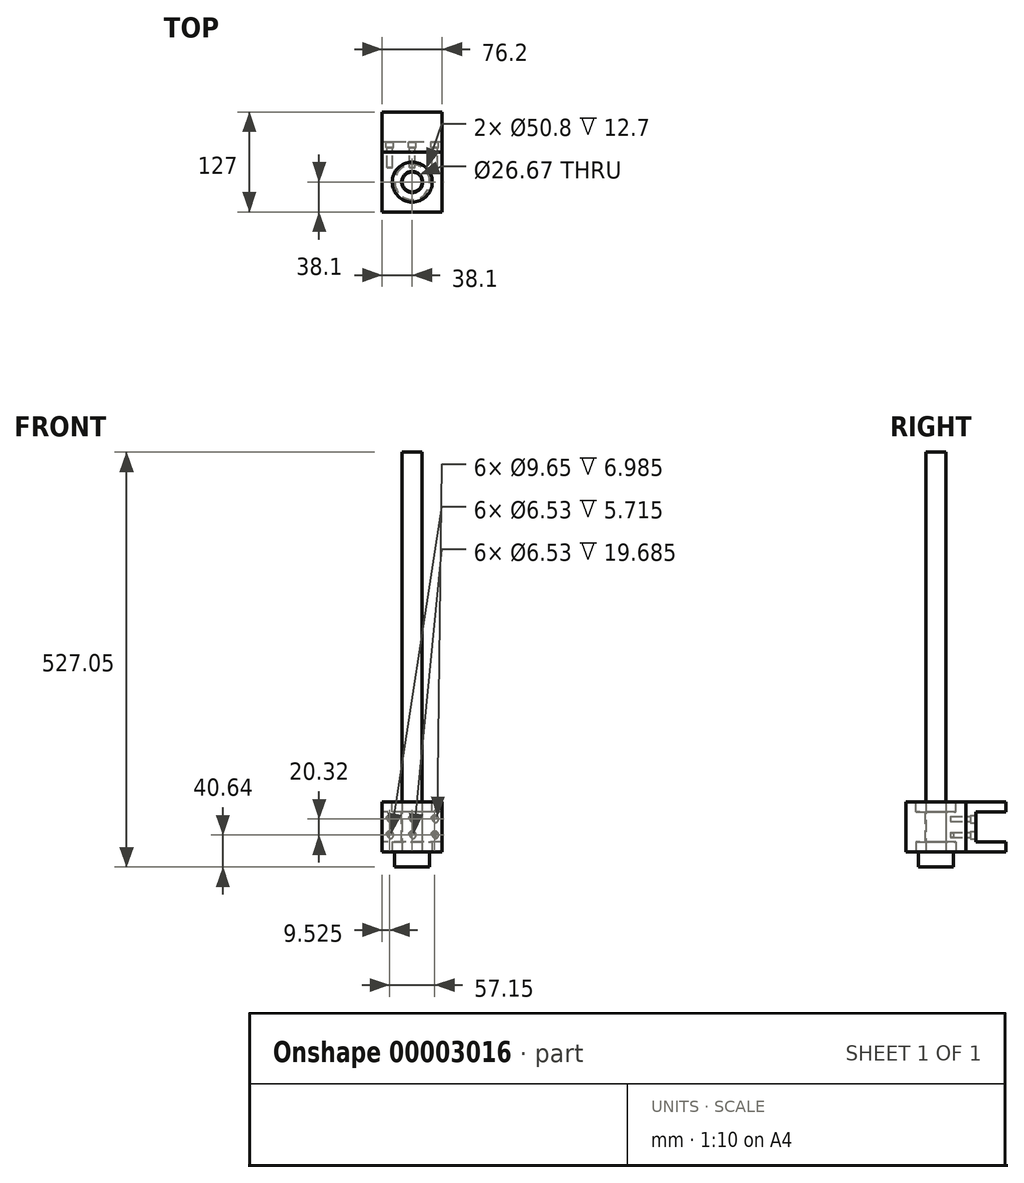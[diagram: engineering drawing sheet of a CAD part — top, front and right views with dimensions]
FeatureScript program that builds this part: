
annotation { "Feature Type Name" : "Feature", "Feature Type Description" : "" }
export const myFeature = defineFeature(function(context is Context, id is Id, definition is map)
    precondition{}
    {
        {
            var Q0;
            Q0=qCreatedBy(makeId("Top.planeOp"),FACE);
            var sketch = newSketch(context, id + "F0", { "sketchPlane" : qUnion([Q0])});
            skLineSegment(sketch, "E0.bottom", {"start": v(0, 0) * mm, "end": v(76.2, 0) * mm});
            skLineSegment(sketch, "E0.top", {"start": v(0, 76.2) * mm, "end": v(76.2, 76.2) * mm});
            skLineSegment(sketch, "E0.left", {"start": v(0, 0) * mm, "end": v(0, 76.2) * mm});
            skLineSegment(sketch, "E0.right", {"start": v(76.2, 0) * mm, "end": v(76.2, 76.2) * mm});
            skSolve(sketch);
        }
        {
            var Q0;
            Q0=makeQuery(id+"F0.imprint","IMPRINT",FACE,{"disambiguationData":[TD([[makeQuery(id+"F0.imprint","IMPRINT",EDGE,{"derivedFrom":sQuery(id+"F0.wireOp",EDGE,"E0.bottom")}),1.0]])]});
            extrude(context, id + "F1", {"entities" : qUnion([Q0]), "depth" : 63.5 * mm});
        }
        {
            var Q0;
            Q0=makeQuery(id+"F1.opExtrude","CAP_FACE",FACE,{"disambiguationData":[OSD([sQuery(id+"F0.wireOp",EDGE,"E0.bottom"),sQuery(id+"F0.wireOp",EDGE,"E0.top"),sQuery(id+"F0.wireOp",EDGE,"E0.left"),sQuery(id+"F0.wireOp",EDGE,"E0.right")])],"isStart":false});
            var sketch = newSketch(context, id + "F2", { "sketchPlane" : qUnion([Q0])});
            skCircle(sketch, "E1", {"center": v(38.1, 38.1) * mm, "radius": 13.34 * mm});
            skSolve(sketch);
        }
        {
            var Q0;
            Q0=makeQuery(id+"F2.imprint","IMPRINT",FACE,{"disambiguationData":[TD([[makeQuery(id+"F2.imprint","IMPRINT",EDGE,{"derivedFrom":sQuery(id+"F2.wireOp",EDGE,"E1")}),1.0]])]});
            extrude(context, id + "F3", {"entities" : qUnion([Q0]), "operationType" : NewBodyOperationType.REMOVE, "endBound" : BoundingType.THROUGH_ALL, "oppositeDirection" : true, "depth" : 25.4 * mm});
        }
        {
            var Q0;
            Q0=makeQuery(id+"F1.opExtrude","CAP_FACE",FACE,{"disambiguationData":[OSD([sQuery(id+"F0.wireOp",EDGE,"E0.bottom"),sQuery(id+"F0.wireOp",EDGE,"E0.top"),sQuery(id+"F0.wireOp",EDGE,"E0.left"),sQuery(id+"F0.wireOp",EDGE,"E0.right")])],"isStart":false});
            var sketch = newSketch(context, id + "F4", { "sketchPlane" : qUnion([Q0])});
            skCircle(sketch, "E2", {"center": v(38.1, 38.1) * mm, "radius": 25.4 * mm});
            skSolve(sketch);
        }
        {
            var Q0;
            Q0=makeQuery(id+"F4.imprint","IMPRINT",FACE,{"disambiguationData":[TD([[makeQuery(id+"F4.imprint","IMPRINT",EDGE,{"derivedFrom":sQuery(id+"F4.wireOp",EDGE,"E2")}),1.0]])]});
            extrude(context, id + "F5", {"entities" : qUnion([Q0]), "operationType" : NewBodyOperationType.REMOVE, "oppositeDirection" : true, "depth" : 12.7 * mm});
        }
        {
            var Q0;
            Q0=makeQuery(id+"F1.opExtrude","CAP_FACE",FACE,{"disambiguationData":[OSD([sQuery(id+"F0.wireOp",EDGE,"E0.bottom"),sQuery(id+"F0.wireOp",EDGE,"E0.top"),sQuery(id+"F0.wireOp",EDGE,"E0.left"),sQuery(id+"F0.wireOp",EDGE,"E0.right")])],"isStart":true});
            var sketch = newSketch(context, id + "F6", { "sketchPlane" : qUnion([Q0])});
            skCircle(sketch, "E3", {"center": v(38.1, -38.1) * mm, "radius": 25.4 * mm});
            skSolve(sketch);
        }
        {
            var Q0;
            Q0=makeQuery(id+"F6.imprint","IMPRINT",FACE,{"disambiguationData":[TD([[makeQuery(id+"F6.imprint","IMPRINT",EDGE,{"derivedFrom":sQuery(id+"F6.wireOp",EDGE,"E3")}),1.0]])]});
            extrude(context, id + "F7", {"entities" : qUnion([Q0]), "operationType" : NewBodyOperationType.REMOVE, "oppositeDirection" : true, "depth" : 12.7 * mm});
        }
        {
            var Q0;
            Q0=makeQuery(id+"F1.opExtrude","CAP_FACE",FACE,{"disambiguationData":[OSD([sQuery(id+"F0.wireOp",EDGE,"E0.bottom"),sQuery(id+"F0.wireOp",EDGE,"E0.top"),sQuery(id+"F0.wireOp",EDGE,"E0.left"),sQuery(id+"F0.wireOp",EDGE,"E0.right")])],"isStart":true});
            var sketch = newSketch(context, id + "F8", { "sketchPlane" : qUnion([Q0])});
            skLineSegment(sketch, "E4.bottom", {"start": v(76.2, 0) * mm, "end": v(0, 0) * mm});
            skLineSegment(sketch, "E4.top", {"start": v(76.2, -76.2) * mm, "end": v(0, -76.2) * mm});
            skLineSegment(sketch, "E4.left", {"start": v(76.2, 0) * mm, "end": v(76.2, -76.2) * mm});
            skLineSegment(sketch, "E4.right", {"start": v(0, 0) * mm, "end": v(0, -76.2) * mm});
            skSolve(sketch);
        }
        {
            var Q0;
            Q0=makeQuery(id+"F8.imprint","IMPRINT",FACE,{"disambiguationData":[TD([[makeQuery(id+"F8.imprint","IMPRINT",EDGE,{"derivedFrom":sQuery(id+"F8.wireOp",EDGE,"E4.bottom")}),-1.0]])]});
            var sketch = newSketch(context, id + "F9", { "sketchPlane" : qUnion([Q0])});
            skCircle(sketch, "E5", {"center": v(38.1, -38.1) * mm, "radius": 12.7 * mm});
            skSolve(sketch);
        }
        {
            var Q0;
            Q0=makeQuery(id+"F9.imprint","IMPRINT",FACE,{"disambiguationData":[TD([[makeQuery(id+"F9.imprint","IMPRINT",EDGE,{"derivedFrom":sQuery(id+"F9.wireOp",EDGE,"E5")}),1.0]])]});
            extrude(context, id + "F10", {"entities" : qUnion([Q0]), "oppositeDirection" : true, "depth" : 508 * mm});
        }
        {
            var Q0;
            Q0=makeQuery(id+"F8.imprint","IMPRINT",FACE,{"disambiguationData":[TD([[makeQuery(id+"F8.imprint","IMPRINT",EDGE,{"derivedFrom":sQuery(id+"F8.wireOp",EDGE,"E4.bottom")}),-1.0]])]});
            var sketch = newSketch(context, id + "F11", { "sketchPlane" : qUnion([Q0])});
            skCircle(sketch, "E6", {"center": v(38.1, -38.1) * mm, "radius": 22.23 * mm});
            skSolve(sketch);
        }
        {
            var Q0;
            Q0=makeQuery(id+"F11.imprint","IMPRINT",FACE,{"disambiguationData":[TD([[makeQuery(id+"F11.imprint","IMPRINT",EDGE,{"derivedFrom":sQuery(id+"F11.wireOp",EDGE,"E6")}),1.0]])]});
            extrude(context, id + "F12", {"entities" : qUnion([Q0]), "depth" : 19.05 * mm});
        }
        {
            var Q0;
            Q0=makeQuery(id+"F1.opExtrude","SWEPT_FACE",FACE,{"disambiguationData":[OSD([sQuery(id+"F0.wireOp",EDGE,"E0.top")])]});
            var sketch = newSketch(context, id + "F13", { "sketchPlane" : qUnion([Q0])});
            skLineSegment(sketch, "E7.bottom", {"start": v(0, 0) * mm, "end": v(-76.2, 0) * mm});
            skLineSegment(sketch, "E7.top", {"start": v(0, 63.5) * mm, "end": v(-76.2, 63.5) * mm});
            skLineSegment(sketch, "E7.left", {"start": v(0, 0) * mm, "end": v(0, 63.5) * mm});
            skLineSegment(sketch, "E7.right", {"start": v(-76.2, 0) * mm, "end": v(-76.2, 63.5) * mm});
            skSolve(sketch);
        }
        {
            var Q0;
            Q0=makeQuery(id+"F13.imprint","IMPRINT",FACE,{"disambiguationData":[TD([[makeQuery(id+"F13.imprint","IMPRINT",EDGE,{"derivedFrom":sQuery(id+"F13.wireOp",EDGE,"E7.bottom")}),-1.0]])]});
            extrude(context, id + "F14", {"entities" : qUnion([Q0]), "depth" : 12.7 * mm});
        }
        {
            var Q0;
            Q0=makeQuery(id+"F14.opExtrude","CAP_FACE",FACE,{"disambiguationData":[OSD([sQuery(id+"F13.wireOp",EDGE,"E7.bottom"),sQuery(id+"F13.wireOp",EDGE,"E7.top"),sQuery(id+"F13.wireOp",EDGE,"E7.left"),sQuery(id+"F13.wireOp",EDGE,"E7.right")])],"isStart":false});
            var sketch = newSketch(context, id + "F15", { "sketchPlane" : qUnion([Q0])});
            skLineSegment(sketch, "E8.bottom", {"start": v(-76.2, 0) * mm, "end": v(0, 0) * mm});
            skLineSegment(sketch, "E8.top", {"start": v(-76.2, 12.7) * mm, "end": v(0, 12.7) * mm});
            skLineSegment(sketch, "E8.left", {"start": v(-76.2, 0) * mm, "end": v(-76.2, 12.7) * mm});
            skLineSegment(sketch, "E8.right", {"start": v(0, 0) * mm, "end": v(0, 12.7) * mm});
            skLineSegment(sketch, "E9.bottom", {"start": v(-76.2, 63.5) * mm, "end": v(0, 63.5) * mm});
            skLineSegment(sketch, "E9.top", {"start": v(-76.2, 50.8) * mm, "end": v(0, 50.8) * mm});
            skLineSegment(sketch, "E9.left", {"start": v(-76.2, 63.5) * mm, "end": v(-76.2, 50.8) * mm});
            skLineSegment(sketch, "E9.right", {"start": v(0, 63.5) * mm, "end": v(0, 50.8) * mm});
            skSolve(sketch);
        }
        {
            var Q0;
            Q0=makeQuery(id+"F15.imprint","IMPRINT",FACE,{"disambiguationData":[TD([[makeQuery(id+"F15.imprint","IMPRINT",EDGE,{"derivedFrom":sQuery(id+"F15.wireOp",EDGE,"E8.bottom")}),-1.0]])]});
            var Q1;
            Q1=makeQuery(id+"F15.imprint","IMPRINT",FACE,{"disambiguationData":[TD([[makeQuery(id+"F15.imprint","IMPRINT",EDGE,{"derivedFrom":sQuery(id+"F15.wireOp",EDGE,"E9.bottom")}),1.0]])]});
            extrude(context, id + "F16", {"entities" : qUnion([Q0, Q1]), "operationType" : NewBodyOperationType.ADD, "depth" : 38.1 * mm});
        }
        {
            var Q0;
            Q0=makeQuery(id+"F14.opExtrude","CAP_FACE",FACE,{"disambiguationData":[OSD([sQuery(id+"F13.wireOp",EDGE,"E7.bottom"),sQuery(id+"F13.wireOp",EDGE,"E7.top"),sQuery(id+"F13.wireOp",EDGE,"E7.left"),sQuery(id+"F13.wireOp",EDGE,"E7.right")])],"isStart":false});
            var sketch = newSketch(context, id + "F17", { "sketchPlane" : qUnion([Q0])});
            skCircle(sketch, "E10", {"center": v(-66.67, 21.59) * mm, "radius": 2.55 * mm});
            skCircle(sketch, "E11", {"center": v(-38.1, 21.59) * mm, "radius": 2.55 * mm});
            skCircle(sketch, "E12", {"center": v(-9.53, 21.59) * mm, "radius": 2.55 * mm});
            skCircle(sketch, "E13", {"center": v(-9.53, 41.91) * mm, "radius": 2.55 * mm});
            skCircle(sketch, "E14", {"center": v(-38.1, 41.91) * mm, "radius": 2.55 * mm});
            skCircle(sketch, "E15", {"center": v(-66.67, 41.91) * mm, "radius": 2.55 * mm});
            skSolve(sketch);
        }
        {
            var Q0;
            Q0=makeQuery(id+"F17.imprint","IMPRINT",FACE,{"disambiguationData":[TD([[makeQuery(id+"F17.imprint","IMPRINT",EDGE,{"derivedFrom":sQuery(id+"F17.wireOp",EDGE,"E10")}),1.0]])]});
            var Q1;
            Q1=makeQuery(id+"F17.imprint","IMPRINT",FACE,{"disambiguationData":[TD([[makeQuery(id+"F17.imprint","IMPRINT",EDGE,{"derivedFrom":sQuery(id+"F17.wireOp",EDGE,"E11")}),1.0]])]});
            var Q2;
            Q2=makeQuery(id+"F17.imprint","IMPRINT",FACE,{"disambiguationData":[TD([[makeQuery(id+"F17.imprint","IMPRINT",EDGE,{"derivedFrom":sQuery(id+"F17.wireOp",EDGE,"E12")}),1.0]])]});
            var Q3;
            Q3=makeQuery(id+"F17.imprint","IMPRINT",FACE,{"disambiguationData":[TD([[makeQuery(id+"F17.imprint","IMPRINT",EDGE,{"derivedFrom":sQuery(id+"F17.wireOp",EDGE,"E13")}),1.0]])]});
            var Q4;
            Q4=makeQuery(id+"F17.imprint","IMPRINT",FACE,{"disambiguationData":[TD([[makeQuery(id+"F17.imprint","IMPRINT",EDGE,{"derivedFrom":sQuery(id+"F17.wireOp",EDGE,"E14")}),1.0]])]});
            var Q5;
            Q5=makeQuery(id+"F17.imprint","IMPRINT",FACE,{"disambiguationData":[TD([[makeQuery(id+"F17.imprint","IMPRINT",EDGE,{"derivedFrom":sQuery(id+"F17.wireOp",EDGE,"E15")}),1.0]])]});
            extrude(context, id + "F18", {"entities" : qUnion([Q0, Q1, Q2, Q3, Q4, Q5]), "operationType" : NewBodyOperationType.REMOVE, "oppositeDirection" : true, "depth" : 28.57 * mm});
        }
        {
            var Q0;
            Q0=makeQuery(id+"F14.opExtrude","CAP_FACE",FACE,{"disambiguationData":[OSD([sQuery(id+"F13.wireOp",EDGE,"E7.bottom"),sQuery(id+"F13.wireOp",EDGE,"E7.top"),sQuery(id+"F13.wireOp",EDGE,"E7.left"),sQuery(id+"F13.wireOp",EDGE,"E7.right")])],"isStart":false});
            var sketch = newSketch(context, id + "F19", { "sketchPlane" : qUnion([Q0])});
            skCircle(sketch, "E16", {"center": v(-9.53, 21.59) * mm, "radius": 4.83 * mm});
            skCircle(sketch, "E17.0.1.0", {"center": v(-9.53, 41.91) * mm, "radius": 4.83 * mm});
            skCircle(sketch, "E17.1.0.0", {"center": v(-38.1, 21.59) * mm, "radius": 4.83 * mm});
            skCircle(sketch, "E17.1.1.0", {"center": v(-38.1, 41.91) * mm, "radius": 4.83 * mm});
            skCircle(sketch, "E17.2.0.0", {"center": v(-66.68, 21.59) * mm, "radius": 4.83 * mm});
            skCircle(sketch, "E17.2.1.0", {"center": v(-66.68, 41.91) * mm, "radius": 4.83 * mm});
            skLineSegment(sketch, "E17.direction1", {"start": v(-9.53, 21.59) * mm, "end": v(-38.1, 21.59) * mm, "construction": true});
            skLineSegment(sketch, "E17.direction2", {"start": v(-9.53, 21.59) * mm, "end": v(-9.53, 41.91) * mm, "construction": true});
            skSolve(sketch);
        }
        {
            var Q0;
            Q0=makeQuery(id+"F19.imprint","IMPRINT",FACE,{"disambiguationData":[TD([[makeQuery(id+"F19.imprint","IMPRINT",EDGE,{"derivedFrom":sQuery(id+"F19.wireOp",EDGE,"E16")}),1.0]])]});
            var Q1;
            Q1=makeQuery(id+"F19.imprint","IMPRINT",FACE,{"disambiguationData":[TD([[makeQuery(id+"F19.imprint","IMPRINT",EDGE,{"derivedFrom":sQuery(id+"F19.wireOp",EDGE,"E17.1.0.0")}),1.0]])]});
            var Q2;
            Q2=makeQuery(id+"F19.imprint","IMPRINT",FACE,{"disambiguationData":[TD([[makeQuery(id+"F19.imprint","IMPRINT",EDGE,{"derivedFrom":sQuery(id+"F19.wireOp",EDGE,"E17.2.0.0")}),1.0]])]});
            var Q3;
            Q3=makeQuery(id+"F19.imprint","IMPRINT",FACE,{"disambiguationData":[TD([[makeQuery(id+"F19.imprint","IMPRINT",EDGE,{"derivedFrom":sQuery(id+"F19.wireOp",EDGE,"E17.2.1.0")}),1.0]])]});
            var Q4;
            Q4=makeQuery(id+"F19.imprint","IMPRINT",FACE,{"disambiguationData":[TD([[makeQuery(id+"F19.imprint","IMPRINT",EDGE,{"derivedFrom":sQuery(id+"F19.wireOp",EDGE,"E17.1.1.0")}),1.0]])]});
            var Q5;
            Q5=makeQuery(id+"F19.imprint","IMPRINT",FACE,{"disambiguationData":[TD([[makeQuery(id+"F19.imprint","IMPRINT",EDGE,{"derivedFrom":sQuery(id+"F19.wireOp",EDGE,"E17.0.1.0")}),1.0]])]});
            extrude(context, id + "F20", {"entities" : qUnion([Q0, Q1, Q2, Q3, Q4, Q5]), "operationType" : NewBodyOperationType.REMOVE, "oppositeDirection" : true, "depth" : 7 * mm});
        }
        {
            var Q0;
            Q0=makeQuery(id+"F20.boolean.opBoolean","COPY",FACE,{"derivedFrom":makeQuery(id+"F20.opExtrude","CAP_FACE",FACE,{"disambiguationData":[OSD([sQuery(id+"F17.wireOp",EDGE,"E10"),sQuery(id+"F19.wireOp",EDGE,"E17.2.0.0")])],"isStart":false})});
            var sketch = newSketch(context, id + "F21", { "sketchPlane" : qUnion([Q0])});
            skCircle(sketch, "E18", {"center": v(-66.67, 21.59) * mm, "radius": 3.26 * mm});
            skCircle(sketch, "E19.0.1.0", {"center": v(-66.67, 41.91) * mm, "radius": 3.26 * mm});
            skCircle(sketch, "E19.1.0.0", {"center": v(-38.1, 21.59) * mm, "radius": 3.26 * mm});
            skCircle(sketch, "E19.1.1.0", {"center": v(-38.1, 41.91) * mm, "radius": 3.26 * mm});
            skCircle(sketch, "E19.2.0.0", {"center": v(-9.52, 21.59) * mm, "radius": 3.26 * mm});
            skCircle(sketch, "E19.2.1.0", {"center": v(-9.52, 41.91) * mm, "radius": 3.26 * mm});
            skLineSegment(sketch, "E19.direction1", {"start": v(-66.67, 21.59) * mm, "end": v(-38.1, 21.59) * mm, "construction": true});
            skLineSegment(sketch, "E19.direction2", {"start": v(-66.67, 21.59) * mm, "end": v(-66.67, 41.91) * mm, "construction": true});
            skSolve(sketch);
        }
        {
            var Q0;
            Q0=makeQuery(id+"F21.imprint","IMPRINT",FACE,{"disambiguationData":[TD([[makeQuery(id+"F21.imprint","IMPRINT",EDGE,{"derivedFrom":sQuery(id+"F21.wireOp",EDGE,"E18")}),1.0]])]});
            var Q1;
            Q1=makeQuery(id+"F21.imprint","IMPRINT",FACE,{"disambiguationData":[TD([[makeQuery(id+"F21.imprint","IMPRINT",EDGE,{"derivedFrom":sQuery(id+"F21.wireOp",EDGE,"E19.0.1.0")}),1.0]])]});
            var Q2;
            Q2=makeQuery(id+"F21.imprint","IMPRINT",FACE,{"disambiguationData":[TD([[makeQuery(id+"F21.imprint","IMPRINT",EDGE,{"derivedFrom":sQuery(id+"F21.wireOp",EDGE,"E19.1.0.0")}),1.0]])]});
            var Q3;
            Q3=makeQuery(id+"F21.imprint","IMPRINT",FACE,{"disambiguationData":[TD([[makeQuery(id+"F21.imprint","IMPRINT",EDGE,{"derivedFrom":sQuery(id+"F21.wireOp",EDGE,"E19.1.1.0")}),1.0]])]});
            var Q4;
            Q4=makeQuery(id+"F21.imprint","IMPRINT",FACE,{"disambiguationData":[TD([[makeQuery(id+"F21.imprint","IMPRINT",EDGE,{"derivedFrom":sQuery(id+"F21.wireOp",EDGE,"E19.2.1.0")}),1.0]])]});
            var Q5;
            Q5=makeQuery(id+"F21.imprint","IMPRINT",FACE,{"disambiguationData":[TD([[makeQuery(id+"F21.imprint","IMPRINT",EDGE,{"derivedFrom":sQuery(id+"F21.wireOp",EDGE,"E19.2.0.0")}),1.0]])]});
            extrude(context, id + "F22", {"entities" : qUnion([Q0, Q1, Q2, Q3, Q4, Q5]), "operationType" : NewBodyOperationType.REMOVE, "oppositeDirection" : true, "depth" : 25.4 * mm});
        }
    });
